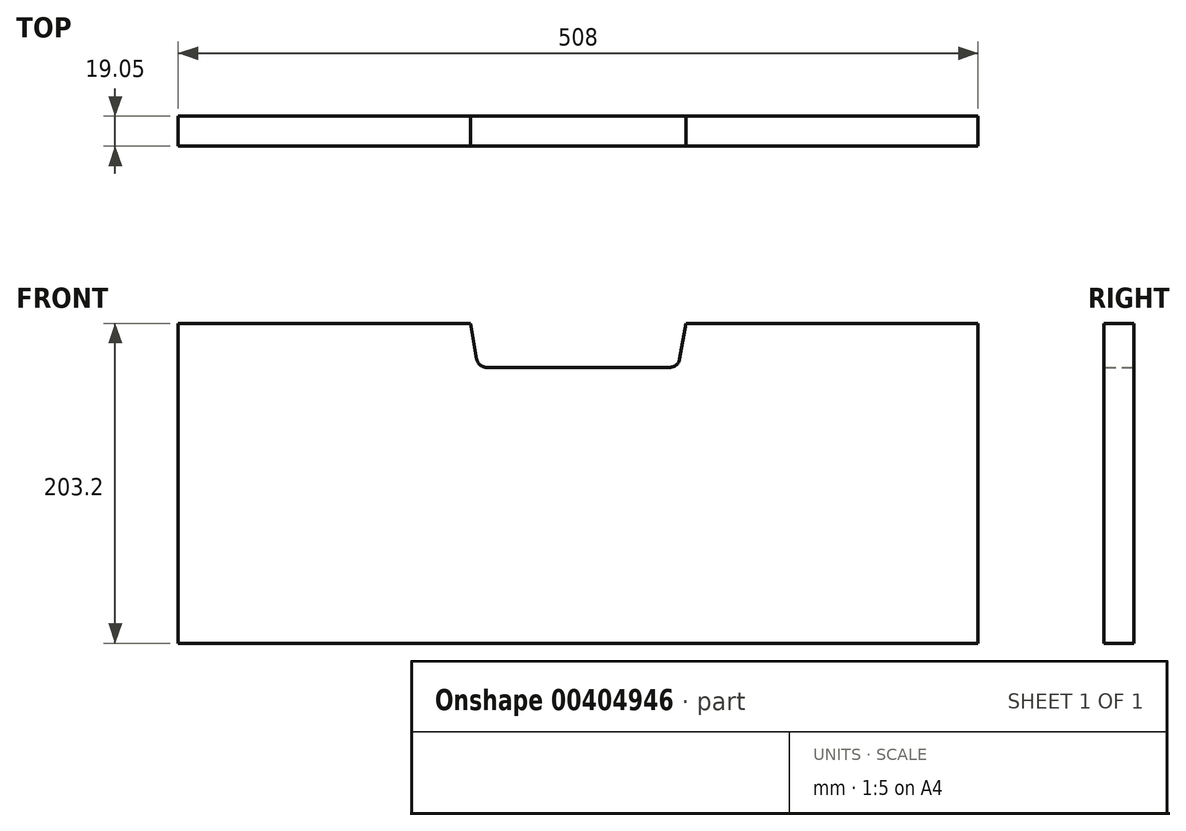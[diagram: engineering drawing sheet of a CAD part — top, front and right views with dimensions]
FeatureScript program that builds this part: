
annotation { "Feature Type Name" : "Feature", "Feature Type Description" : "" }
export const myFeature = defineFeature(function(context is Context, id is Id, definition is map)
    precondition{}
    {
        {
            var Q0;
            Q0=qCreatedBy(makeId("Front.planeOp"),FACE);
            var sketch = newSketch(context, id + "F0", { "sketchPlane" : qUnion([Q0])});
            skLineSegment(sketch, "E0", {"start": v(-254, 101.6) * mm, "end": v(-254, -101.6) * mm});
            skLineSegment(sketch, "E1", {"start": v(-254, -101.6) * mm, "end": v(254, -101.6) * mm});
            skLineSegment(sketch, "E2", {"start": v(254, -101.6) * mm, "end": v(254, 101.6) * mm});
            skLineSegment(sketch, "E3", {"start": v(254, 101.6) * mm, "end": v(-68.43, 101.6) * mm});
            skLineSegment(sketch, "E4", {"start": v(-68.43, 101.6) * mm, "end": v(-63.5, 73.66) * mm});
            skLineSegment(sketch, "E5", {"start": v(63.5, 73.66) * mm, "end": v(-63.5, 73.66) * mm});
            skLineSegment(sketch, "E6", {"start": v(63.5, 73.66) * mm, "end": v(68.43, 101.6) * mm});
            skLineSegment(sketch, "E7", {"start": v(68.43, 101.6) * mm, "end": v(-254, 101.6) * mm});
            skSolve(sketch);
        }
        {
            var Q0;
            {var subQ0=sQuery(id+"F0.wireOp",EDGE,"E0");Q0=makeQuery(id+"F0.imprint","IMPRINT",FACE,{"disambiguationData":[TD([[makeQuery(id+"F0.imprint","IMPRINT",EDGE,{"derivedFrom":subQ0}),1.0]])]});}
            extrude(context, id + "F1", {"entities" : qUnion([Q0]), "depth" : 19.05 * mm});
        }
        {
            var Q0;
            Q0=makeQuery(id+"F1.opExtrude","SWEPT_EDGE",EDGE,{"disambiguationData":[OSD([sQuery(id+"F0.wireOp",EDGE,"E5"),sQuery(id+"F0.wireOp",EDGE,"E6")])]});
            var Q1;
            Q1=makeQuery(id+"F1.opExtrude","SWEPT_EDGE",EDGE,{"disambiguationData":[OSD([sQuery(id+"F0.wireOp",EDGE,"E4"),sQuery(id+"F0.wireOp",EDGE,"E5")])]});
            fillet(context, id + "F2", {"entities" : qUnion([Q0, Q1]), "radius" : 6.35 * mm, "tangentPropagation" : true, "allowEdgeOverflow" : false});
        }
    });
